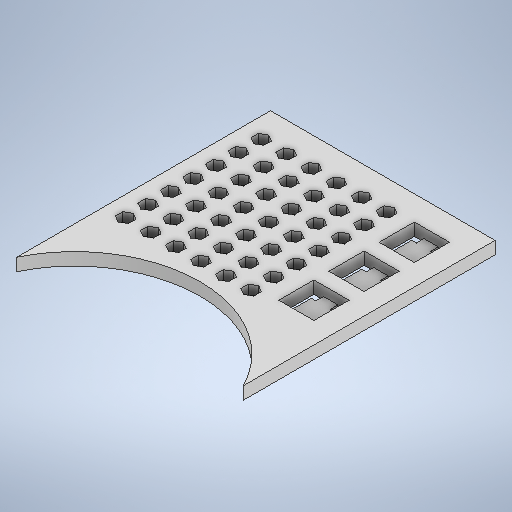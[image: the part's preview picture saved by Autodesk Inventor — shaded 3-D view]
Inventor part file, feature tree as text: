
AUTODESK INVENTOR PART (.ipt)
format: ipt  version: 2025.2 (Build 292293000, 293)  size: 1,250,304 bytes
history: native  units: mm
features: extrude x5, other x3, sketch x3
ambient origin geometry x8: Origin, YZ Plane, XZ Plane, XY Plane, X Axis, Y Axis, Z Axis, Center Point
bodies: Body1 (feature_tree)
feature tree (11):
  other  "Bryła1"
  extrude  "Wyciągnięcie proste1"  Depth=50.0mm
  sketch  "Szkic2"
  extrude  "Wyciągnięcie proste2"  Depth=5.0mm TaperAngle=0.0deg
  extrude  "Wyciągnięcie proste3"  Depth=14.0mm
  extrude  "Wyciągnięcie proste4"  Depth=14.0mm
  extrude  "Wyciągnięcie proste5"  Depth=30.0mm
  sketch  "Szkic1"
  other  "Prostokątny szyk szkicu1"
  sketch  "Szkic3"
  other  "Prostokątny szyk szkicu2"
